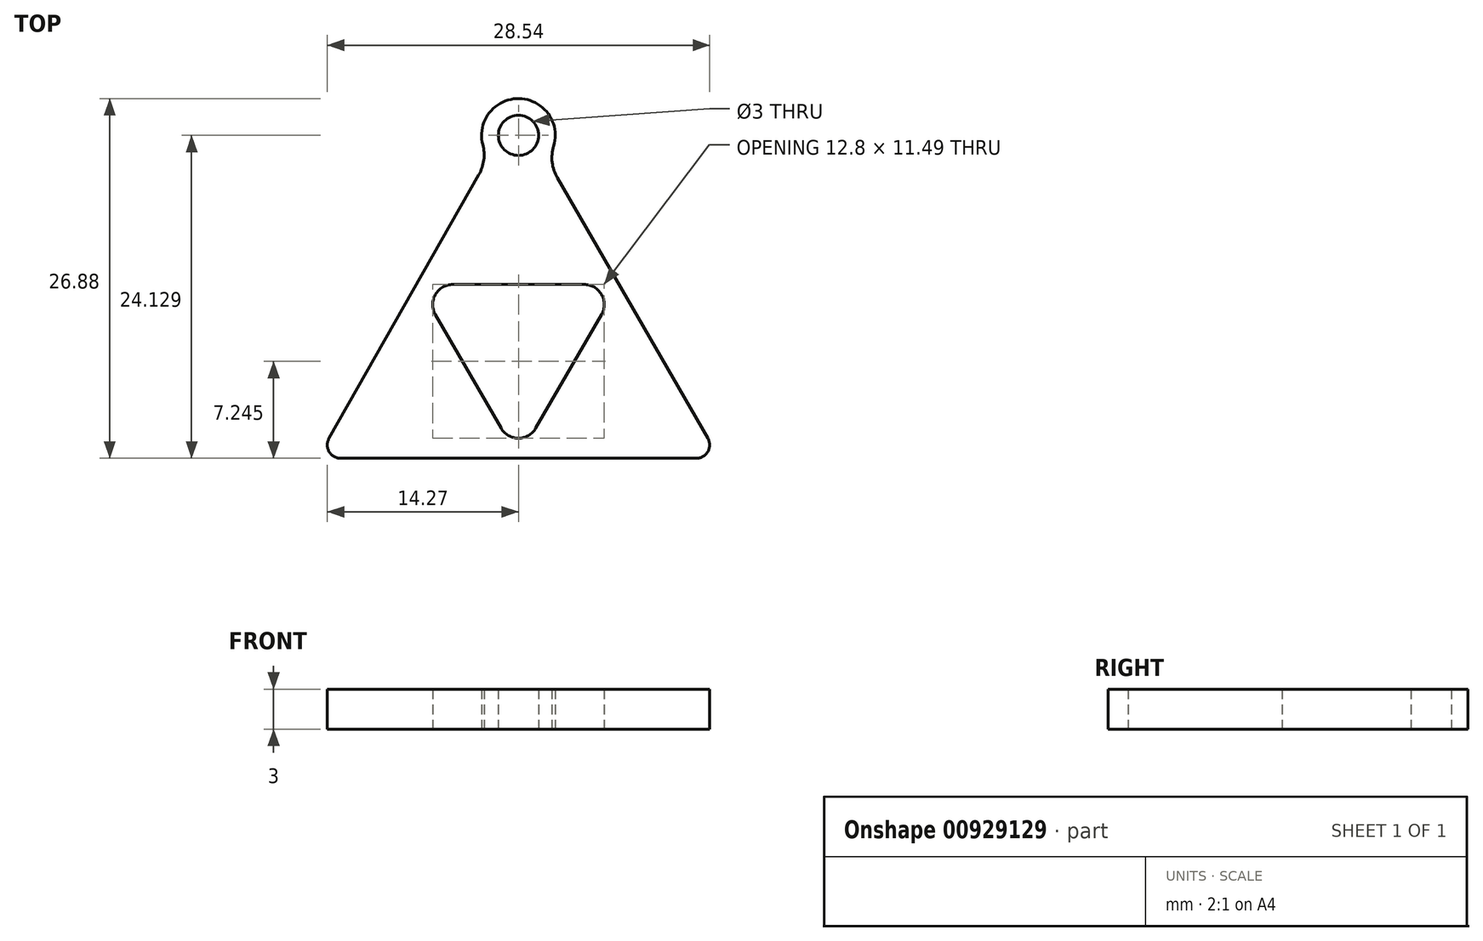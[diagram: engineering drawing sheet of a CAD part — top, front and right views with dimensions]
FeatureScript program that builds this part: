
annotation { "Feature Type Name" : "Feature", "Feature Type Description" : "" }
export const myFeature = defineFeature(function(context is Context, id is Id, definition is map)
    precondition{}
    {
        {
            var Q0;
            Q0=qCreatedBy(makeId("Top.planeOp"),FACE);
            var sketch = newSketch(context, id + "F0", { "sketchPlane" : qUnion([Q0])});
            skLineSegment(sketch, "E0", {"start": v(-13.27, -8.66) * mm, "end": v(13.27, -8.66) * mm});
            skLineSegment(sketch, "E1", {"start": v(14.13, -7.16) * mm, "end": v(2.1, 13.69) * mm});
            skLineSegment(sketch, "E2", {"start": v(-7.5, 4.33) * mm, "end": v(15, -8.66) * mm, "construction": true});
            skLineSegment(sketch, "E3", {"start": v(7.5, 4.33) * mm, "end": v(-15, -8.66) * mm, "construction": true});
            skLineSegment(sketch, "E4", {"start": v(0, 17.32) * mm, "end": v(0, -8.66) * mm, "construction": true});
            skPoint(sketch, "E5", {"position": v(0, 0) * mm});
            skLineSegment(sketch, "E6", {"start": v(4.9, 4.33) * mm, "end": v(-4.9, 4.33) * mm});
            skLineSegment(sketch, "E7", {"start": v(-6.2, 2.08) * mm, "end": v(-1.3, -6.41) * mm});
            skLineSegment(sketch, "E8", {"start": v(6.2, 2.08) * mm, "end": v(1.3, -6.41) * mm});
            skPoint(sketch, "E9.visualSharp", {"position": v(-7.5, 4.33) * mm});
            skArc(sketch, "E9.filletArc", {"start": v(-4.9, 4.33) * mm, "mid": v(-6.2, 3.58) * mm, "end": v(-6.2, 2.08) * mm});
            skPoint(sketch, "E10.visualSharp", {"position": v(7.5, 4.33) * mm});
            skArc(sketch, "E10.filletArc", {"start": v(6.2, 2.08) * mm, "mid": v(6.2, 3.58) * mm, "end": v(4.9, 4.33) * mm});
            skPoint(sketch, "E11.visualSharp", {"position": v(0, -8.66) * mm});
            skArc(sketch, "E11.filletArc", {"start": v(-1.3, -6.41) * mm, "mid": v(0, -7.16) * mm, "end": v(1.3, -6.41) * mm});
            skPoint(sketch, "E12.visualSharp", {"position": v(0, 17.32) * mm});
            skPoint(sketch, "E13.visualSharp", {"position": v(15, -8.66) * mm});
            skArc(sketch, "E13.filletArc", {"start": v(13.27, -8.66) * mm, "mid": v(14.13, -8.16) * mm, "end": v(14.13, -7.16) * mm});
            skPoint(sketch, "E14.visualSharp", {"position": v(-15, -8.66) * mm});
            skArc(sketch, "E14.filletArc", {"start": v(-14.13, -7.16) * mm, "mid": v(-14.13, -8.16) * mm, "end": v(-13.27, -8.66) * mm});
            skArc(sketch, "E15", {"start": v(2.1, 13.69) * mm, "mid": v(0.1, 18.22) * mm, "end": v(-2.21, 13.84) * mm});
            skCircle(sketch, "E16", {"center": v(0, 15.47) * mm, "radius": 1.5 * mm});
            skLineSegment(sketch, "E17.trimOffspring", {"start": v(-2.21, 13.84) * mm, "end": v(-14.13, -7.16) * mm});
            skSolve(sketch);
        }
        {
            var Q0;
            Q0=makeQuery(id+"F0.imprint","IMPRINT",FACE,{"disambiguationData":[TD([[makeQuery(id+"F0.imprint","IMPRINT",EDGE,{"derivedFrom":sQuery(id+"F0.wireOp",EDGE,"A11opOZI-jZWe-JnCO-Zkhr-LAuPJn6n7dkP")}),1.0]])]});
            var Q1;
            Q1=makeQuery(id+"F0.imprint","IMPRINT",FACE,{"disambiguationData":[TD([[makeQuery(id+"F0.imprint","IMPRINT",EDGE,{"derivedFrom":sQuery(id+"F0.wireOp",EDGE,"E0")}),1.0]])]});
            extrude(context, id + "F1", {"entities" : qUnion([Q0, Q1]), "depth" : 3 * mm, "offsetDistance" : 25 * mm});
        }
        {
            var Q0;
            Q0=makeQuery(id+"F1.opExtrude","SWEPT_EDGE",EDGE,{"disambiguationData":[OSD([sQuery(id+"F0.wireOp",EDGE,"E15"),sQuery(id+"F0.wireOp",EDGE,"E17.trimOffspring")])]});
            var Q1;
            Q1=makeQuery(id+"F1.opExtrude","SWEPT_EDGE",EDGE,{"disambiguationData":[OSD([sQuery(id+"F0.wireOp",EDGE,"E1"),sQuery(id+"F0.wireOp",EDGE,"E15")])]});
            fillet(context, id + "F2", {"entities" : qUnion([Q0, Q1]), "radius" : 3 * mm, "tangentPropagation" : true, "allowEdgeOverflow" : false});
        }
    });
